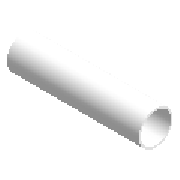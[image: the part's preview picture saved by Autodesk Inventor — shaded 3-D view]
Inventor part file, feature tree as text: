
AUTODESK INVENTOR PART (.ipt)
format: ipt  version: 2025.2 (Build 292293000, 293)  size: 138,240 bytes
history: native  units: mm (DEFAULTED — no unit token found)
features: other x4, extrude x1
ambient origin geometry x8: Origin, YZ Plane, XZ Plane, XY Plane, X Axis, Y Axis, Z Axis, Center Point
bodies: Solid1 (feature_tree)
feature tree (5):
  extrude  "Extrusion1"  Depth=21.336mm
  other  "Work Axis1"
  other  "Work Point1"
  other  "Work Axis2"
  other  "Work Point2"
